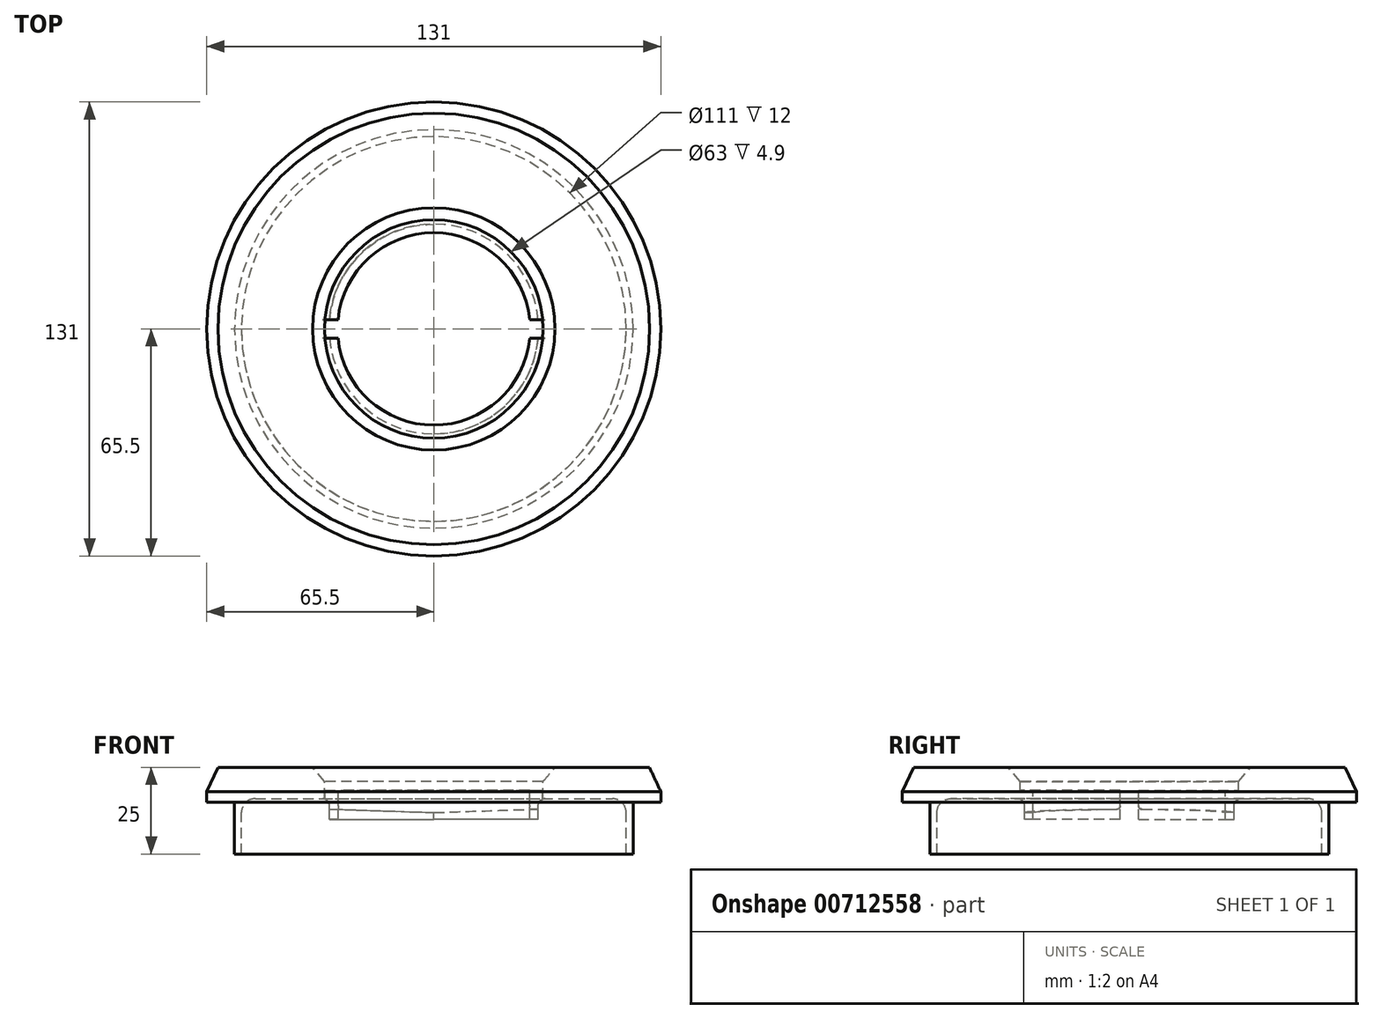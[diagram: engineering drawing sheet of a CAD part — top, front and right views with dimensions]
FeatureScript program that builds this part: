
annotation { "Feature Type Name" : "Feature", "Feature Type Description" : "" }
export const myFeature = defineFeature(function(context is Context, id is Id, definition is map)
    precondition{}
    {
        {
            var Q0;
            Q0=qCreatedBy(makeId("Front.planeOp"),FACE);
            var sketch = newSketch(context, id + "F0", { "sketchPlane" : qUnion([Q0])});
            skLineSegment(sketch, "E0", {"start": v(-65.5, 0) * mm, "end": v(-65.5, -3) * mm});
            skLineSegment(sketch, "E1", {"start": v(-65.5, -3) * mm, "end": v(-57.5, -3) * mm});
            skLineSegment(sketch, "E2", {"start": v(-57.5, -3) * mm, "end": v(-57.5, -18) * mm});
            skLineSegment(sketch, "E3", {"start": v(-57.5, -18) * mm, "end": v(-55.5, -18) * mm});
            skLineSegment(sketch, "E4", {"start": v(-55.5, -2) * mm, "end": v(-55.5, -18) * mm});
            skLineSegment(sketch, "E5", {"start": v(-55.5, -2) * mm, "end": v(-30.25, -2) * mm});
            skLineSegment(sketch, "E6", {"start": v(-30.25, -2) * mm, "end": v(-30.25, -8) * mm});
            skLineSegment(sketch, "E7", {"start": v(-30.25, -8) * mm, "end": v(-27.75, -8) * mm});
            skLineSegment(sketch, "E8", {"start": v(-27.75, -8) * mm, "end": v(-27.75, 0.4) * mm});
            skLineSegment(sketch, "E9", {"start": v(-31.5, 0.4) * mm, "end": v(-27.75, 0.4) * mm});
            skLineSegment(sketch, "E10", {"start": v(-31.5, 0.4) * mm, "end": v(-31.5, 2.9) * mm});
            skLineSegment(sketch, "E11", {"start": v(-31.5, 2.9) * mm, "end": v(-34.94, 7) * mm});
            skLineSegment(sketch, "E12", {"start": v(-34.94, 7) * mm, "end": v(-62.24, 7) * mm});
            skLineSegment(sketch, "E13", {"start": v(-62.24, 7) * mm, "end": v(-65.5, 0) * mm});
            skLineSegment(sketch, "E14", {"start": v(0, 0) * mm, "end": v(0, -29.79) * mm, "construction": true});
            skSolve(sketch);
        }
        {
            var Q0;
            Q0 = qSketchRegion(id + "F0", true);
            var Q1;
            Q1=sQuery(id+"F0.wireOp",EDGE,"E14");
            revolve(context, id + "F1", {"surfaceOperationType" : NewSurfaceOperationType.NEW, "entities" : qUnion([Q0]), "axis" : qUnion([Q1]), "revolveType" : RevolveType.FULL});
        }
        {
            var Q0;
            Q0=makeQuery(id+"F1.opRevolve","SWEPT_FACE",FACE,{"disambiguationData":[OSD([sQuery(id+"F0.wireOp",EDGE,"E9")])]});
            var sketch = newSketch(context, id + "F2", { "sketchPlane" : qUnion([Q0])});
            skLineSegment(sketch, "E15", {"start": v(-31.39, 2.64) * mm, "end": v(31.39, 2.64) * mm});
            skLineSegment(sketch, "E16.MirrorCS", {"start": v(-31.39, -2.64) * mm, "end": v(31.39, -2.64) * mm});
            skArc(sketch, "E17.0", {"start": v(-31.39, 2.64) * mm, "mid": v(-31.5, 0) * mm, "end": v(-31.39, -2.64) * mm});
            skArc(sketch, "E18.trimOffspring", {"start": v(31.39, -2.64) * mm, "mid": v(31.5, 0) * mm, "end": v(31.39, 2.64) * mm});
            skSolve(sketch);
        }
        {
            var Q0;
            Q0 = qSketchRegion(id + "F2", true);
            extrude(context, id + "F3", {"entities" : qUnion([Q0]), "operationType" : NewBodyOperationType.REMOVE, "endBound" : BoundingType.THROUGH_ALL, "oppositeDirection" : true, "depth" : 25 * mm, "offsetDistance" : 25 * mm});
        }
        {
            var Q0;
            Q0=qCreatedBy(makeId("Front.planeOp"),FACE);
            var sketch = newSketch(context, id + "F4", { "sketchPlane" : qUnion([Q0])});
            skLineSegment(sketch, "E19", {"start": v(0, -6) * mm, "end": v(0, -8.05) * mm});
            skLineSegment(sketch, "E20", {"start": v(-30.13, -5) * mm, "end": v(0, -6) * mm});
            skLineSegment(sketch, "E21.0", {"start": v(-30.13, -8) * mm, "end": v(-30.13, -5) * mm});
            skPoint(sketch, "E22.orphan", {"position": v(-30.13, -2) * mm});
            skLineSegment(sketch, "E23", {"start": v(0, -8.05) * mm, "end": v(-30.13, -8) * mm});
            skSolve(sketch);
        }
        {
            var Q0;
            Q0 = qSketchRegion(id + "F4", true);
            extrude(context, id + "F5", {"entities" : qUnion([Q0]), "operationType" : NewBodyOperationType.REMOVE, "oppositeDirection" : true, "depth" : 40 * mm, "offsetDistance" : 25 * mm});
        }
        {
            var Q0;
            Q0=qCreatedBy(makeId("Front.planeOp"),FACE);
            var sketch = newSketch(context, id + "F6", { "sketchPlane" : qUnion([Q0])});
            skLineSegment(sketch, "E24", {"start": v(0, -6) * mm, "end": v(0, -10) * mm});
            skLineSegment(sketch, "E25", {"start": v(0, -10) * mm, "end": v(30.13, -10) * mm});
            skLineSegment(sketch, "E26.0", {"start": v(30.13, -5) * mm, "end": v(30.13, -10) * mm});
            skLineSegment(sketch, "E27", {"start": v(0, -6) * mm, "end": v(30.13, -5) * mm});
            skPoint(sketch, "E28.orphan", {"position": v(30.13, -2) * mm});
            skPoint(sketch, "E29.orphan", {"position": v(30.13, -8) * mm});
            skSolve(sketch);
        }
        {
            var Q0;
            Q0 = qSketchRegion(id + "F6", true);
            extrude(context, id + "F7", {"entities" : qUnion([Q0]), "operationType" : NewBodyOperationType.REMOVE, "depth" : 40 * mm, "offsetDistance" : 25 * mm});
        }
        {
            var Q0;
            Q0=makeQuery(id+"F5.boolean.opBoolean","INTERSECT",EDGE,{"derivedFrom":[makeQuery(id+"F3.boolean.opBoolean","COPY",FACE,{"disambiguationData":[OD(0.0)],"derivedFrom":makeQuery(id+"F3.opExtrude","SWEPT_FACE",FACE,{"disambiguationData":[OSD([sQuery(id+"F2.wireOp",EDGE,"E15")])]})}),makeQuery(id+"F5.opExtrude","SWEPT_FACE",FACE,{"disambiguationData":[OSD([sQuery(id+"F4.wireOp",EDGE,"E20")])]})]});
            var Q1;
            Q1=makeQuery(id+"F7.boolean.opBoolean","INTERSECT",EDGE,{"derivedFrom":[makeQuery(id+"F3.boolean.opBoolean","COPY",FACE,{"disambiguationData":[OD(1.0)],"derivedFrom":makeQuery(id+"F3.opExtrude","SWEPT_FACE",FACE,{"disambiguationData":[OSD([sQuery(id+"F2.wireOp",EDGE,"E16.MirrorCS")])]})}),makeQuery(id+"F7.opExtrude","SWEPT_FACE",FACE,{"disambiguationData":[OSD([sQuery(id+"F6.wireOp",EDGE,"E27")])]})]});
            fillet(context, id + "F8", {"entities" : qUnion([Q0, Q1]), "radius" : 1 * mm, "tangentPropagation" : true, "allowEdgeOverflow" : false});
        }
        {
            var Q0;
            Q0=makeQuery(id+"F1.opRevolve","SWEPT_EDGE",EDGE,{"disambiguationData":[OSD([sQuery(id+"F0.wireOp",EDGE,"E4"),sQuery(id+"F0.wireOp",EDGE,"E5")])]});
            fillet(context, id + "F9", {"entities" : qUnion([Q0]), "radius" : 4 * mm, "tangentPropagation" : true, "allowEdgeOverflow" : false});
        }
        {
            var Q0;
            {var subQ0=sQuery(id+"F0.wireOp",EDGE,"E5");var subQ1=sQuery(id+"F0.wireOp",EDGE,"E6");Q0=makeQuery(id+"F3.boolean.opBoolean","SPLIT",EDGE,{"disambiguationData":[TD([makeQuery(id+"F3.opExtrude","SWEPT_FACE",FACE,{"disambiguationData":[OSD([sQuery(id+"F2.wireOp",EDGE,"E16.MirrorCS")])]})])],"derivedFrom":makeQuery(id+"F1.opRevolve","SWEPT_EDGE",EDGE,{"disambiguationData":[OSD([subQ0,subQ1])]})});}
            var Q1;
            {var subQ0=sQuery(id+"F0.wireOp",EDGE,"E5");var subQ1=sQuery(id+"F0.wireOp",EDGE,"E6");Q1=makeQuery(id+"F3.boolean.opBoolean","SPLIT",EDGE,{"disambiguationData":[TD([makeQuery(id+"F3.opExtrude","SWEPT_FACE",FACE,{"disambiguationData":[OSD([sQuery(id+"F2.wireOp",EDGE,"E15")])]})])],"derivedFrom":makeQuery(id+"F1.opRevolve","SWEPT_EDGE",EDGE,{"disambiguationData":[OSD([subQ0,subQ1])]})});}
            fillet(context, id + "F10", {"entities" : qUnion([Q0, Q1]), "radius" : 2 * mm, "tangentPropagation" : true, "allowEdgeOverflow" : false});
        }
    });
